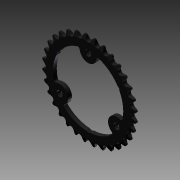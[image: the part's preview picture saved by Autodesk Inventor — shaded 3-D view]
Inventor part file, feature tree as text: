
AUTODESK INVENTOR PART (.ipt)
format: ipt  version: 2012 (Build 160160000, 160)  size: 835,584 bytes
history: native  units: in
note: dims shown in document units (in); Inventor stores cm internally (conversion verified against a paired STEP export)
features: boolean_combine x1, extrude x1, imported_body x1, sketch x1
ambient origin geometry x8: Origin, YZ Plane, XZ Plane, XY Plane, X Axis, Y Axis, Z Axis, Center Point
feature tree (4):
  boolean_combine  "Combine1"
  extrude  "Extrusion1"  [1 undecoded]
  imported_body  "Base1"
  sketch  "Sketch1"  dims[d0=1.0in d1=0.0in]
note: 1 required parameter value undecoded (feature->parameter linkage not recoverable at this tier; creation-order binding heuristic only, values carry confidence <= 0.55)
